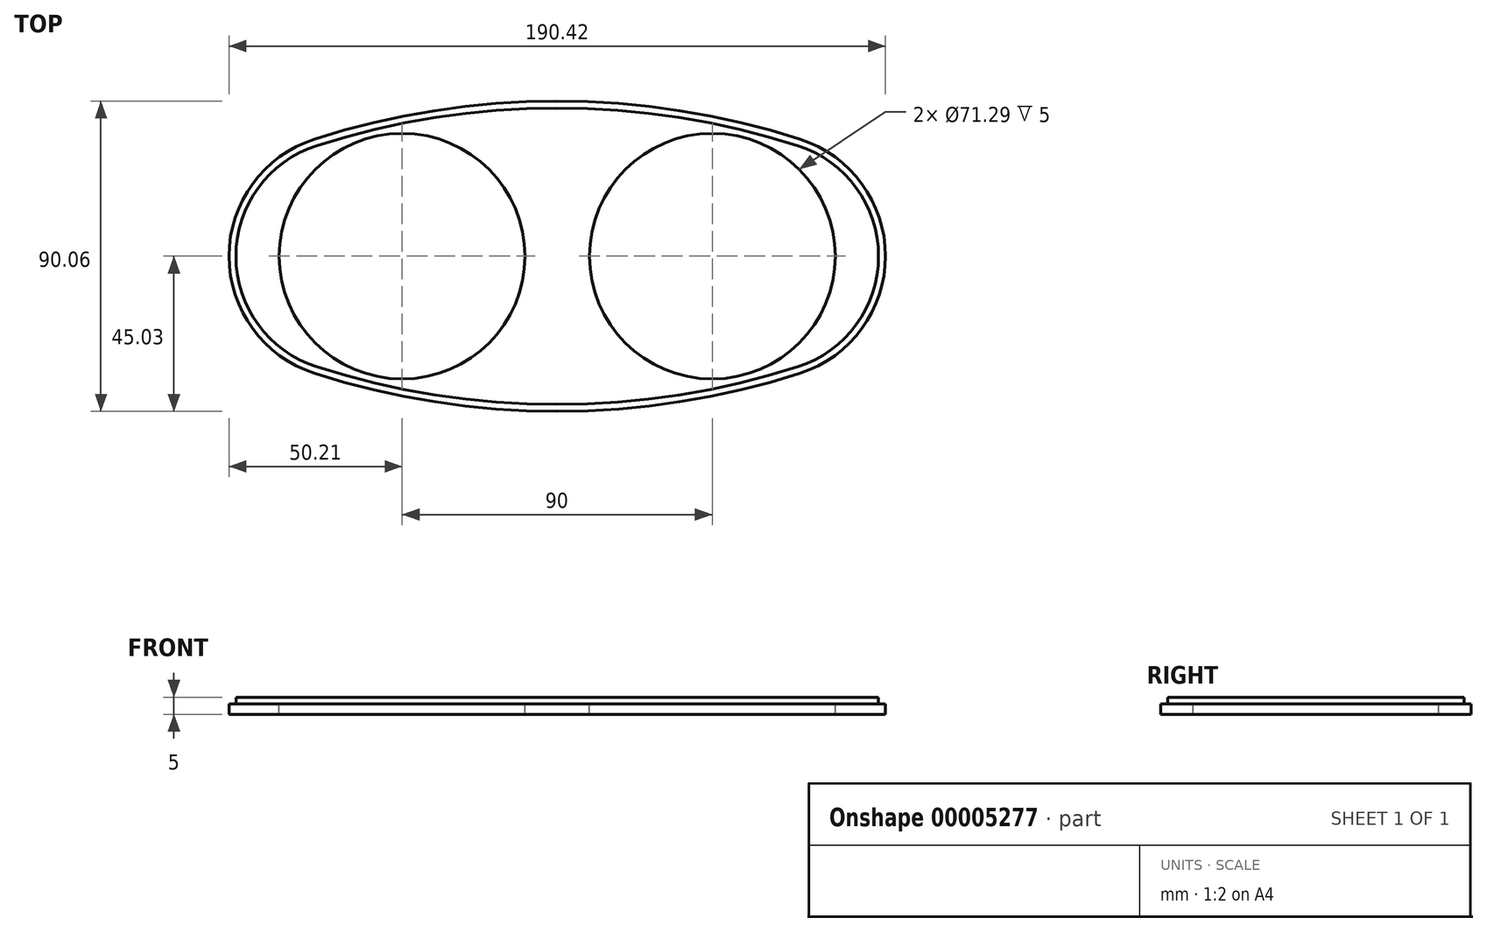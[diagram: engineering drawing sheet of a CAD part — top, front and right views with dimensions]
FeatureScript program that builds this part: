
annotation { "Feature Type Name" : "Feature", "Feature Type Description" : "" }
export const myFeature = defineFeature(function(context is Context, id is Id, definition is map)
    precondition{}
    {
        {
            var Q0;
            Q0=qCreatedBy(makeId("Top.planeOp"),FACE);
            var sketch = newSketch(context, id + "F0", { "sketchPlane" : qUnion([Q0])});
            skArc(sketch, "E0", {"start": v(-70.42, 34) * mm, "mid": v(-95.21, 0) * mm, "end": v(-70.42, -34) * mm});
            skArc(sketch, "E1", {"start": v(70.42, -34) * mm, "mid": v(95.21, 0) * mm, "end": v(70.42, 34) * mm});
            skArc(sketch, "E2", {"start": v(-70.42, -34) * mm, "mid": v(0, -45.03) * mm, "end": v(70.42, -34) * mm});
            skArc(sketch, "E3", {"start": v(70.42, 34) * mm, "mid": v(0, 45.03) * mm, "end": v(-70.42, 34) * mm});
            skSolve(sketch);
        }
        {
            var Q0;
            Q0=makeQuery(id+"F0.imprint","IMPRINT",FACE,{"disambiguationData":[TD([[makeQuery(id+"F0.imprint","IMPRINT",EDGE,{"derivedFrom":sQuery(id+"F0.wireOp",EDGE,"E0")}),1.0]])]});
            extrude(context, id + "F1", {"entities" : qUnion([Q0]), "depth" : 3 * mm});
        }
        {
            var Q0;
            Q0=makeQuery(id+"F1.opExtrude","CAP_FACE",FACE,{"disambiguationData":[OSD([sQuery(id+"F0.wireOp",EDGE,"E0"),sQuery(id+"F0.wireOp",EDGE,"E1"),sQuery(id+"F0.wireOp",EDGE,"E2"),sQuery(id+"F0.wireOp",EDGE,"E3")])],"isStart":false});
            var sketch = newSketch(context, id + "F2", { "sketchPlane" : qUnion([Q0])});
            skArc(sketch, "E4.0", {"start": v(69.81, 32.1) * mm, "mid": v(0, 43.03) * mm, "end": v(-69.81, 32.1) * mm});
            skArc(sketch, "E4.1", {"start": v(69.81, -32.1) * mm, "mid": v(93.21, 0) * mm, "end": v(69.81, 32.1) * mm});
            skArc(sketch, "E4.2", {"start": v(-69.81, -32.1) * mm, "mid": v(0, -43.03) * mm, "end": v(69.81, -32.1) * mm});
            skArc(sketch, "E4.3", {"start": v(-69.81, 32.1) * mm, "mid": v(-93.21, 0) * mm, "end": v(-69.81, -32.1) * mm});
            skSolve(sketch);
        }
        {
            var Q0;
            Q0=makeQuery(id+"F2.imprint","IMPRINT",FACE,{"disambiguationData":[TD([[makeQuery(id+"F2.imprint","IMPRINT",EDGE,{"derivedFrom":sQuery(id+"F2.wireOp",EDGE,"E4.0")}),1.0]])]});
            extrude(context, id + "F3", {"entities" : qUnion([Q0]), "operationType" : NewBodyOperationType.ADD, "depth" : 2 * mm});
        }
        {
            var Q0;
            Q0=makeQuery(id+"F3.opExtrude","CAP_FACE",FACE,{"disambiguationData":[OSD([sQuery(id+"F2.wireOp",EDGE,"E4.0"),sQuery(id+"F2.wireOp",EDGE,"E4.1"),sQuery(id+"F2.wireOp",EDGE,"E4.2"),sQuery(id+"F2.wireOp",EDGE,"E4.3")])],"isStart":false});
            var sketch = newSketch(context, id + "F4", { "sketchPlane" : qUnion([Q0])});
            skCircle(sketch, "E5", {"center": v(-45, 0) * mm, "radius": 37.65 * mm, "construction": true});
            skCircle(sketch, "E6", {"center": v(45, 0) * mm, "radius": 37.65 * mm, "construction": true});
            skCircle(sketch, "E7.0", {"center": v(-45, 0) * mm, "radius": 35.65 * mm});
            skCircle(sketch, "E8.0", {"center": v(45, 0) * mm, "radius": 35.65 * mm});
            skSolve(sketch);
        }
        {
            var Q0;
            {Q0=qUnion([makeQuery(id+"F4.imprint","IMPRINT",FACE,{"disambiguationData":[TD([[makeQuery(id+"F4.imprint","IMPRINT",EDGE,{"derivedFrom":sQuery(id+"F4.wireOp",EDGE,"E7.0")}),1.0]])]}),makeQuery(id+"F4.imprint","IMPRINT",FACE,{"disambiguationData":[TD([[makeQuery(id+"F4.imprint","IMPRINT",EDGE,{"derivedFrom":sQuery(id+"F4.wireOp",EDGE,"E8.0")}),1.0]])]})]);}
            extrude(context, id + "F5", {"entities" : qUnion([Q0]), "operationType" : NewBodyOperationType.REMOVE, "endBound" : BoundingType.THROUGH_ALL, "oppositeDirection" : true, "depth" : 25 * mm});
        }
    });
